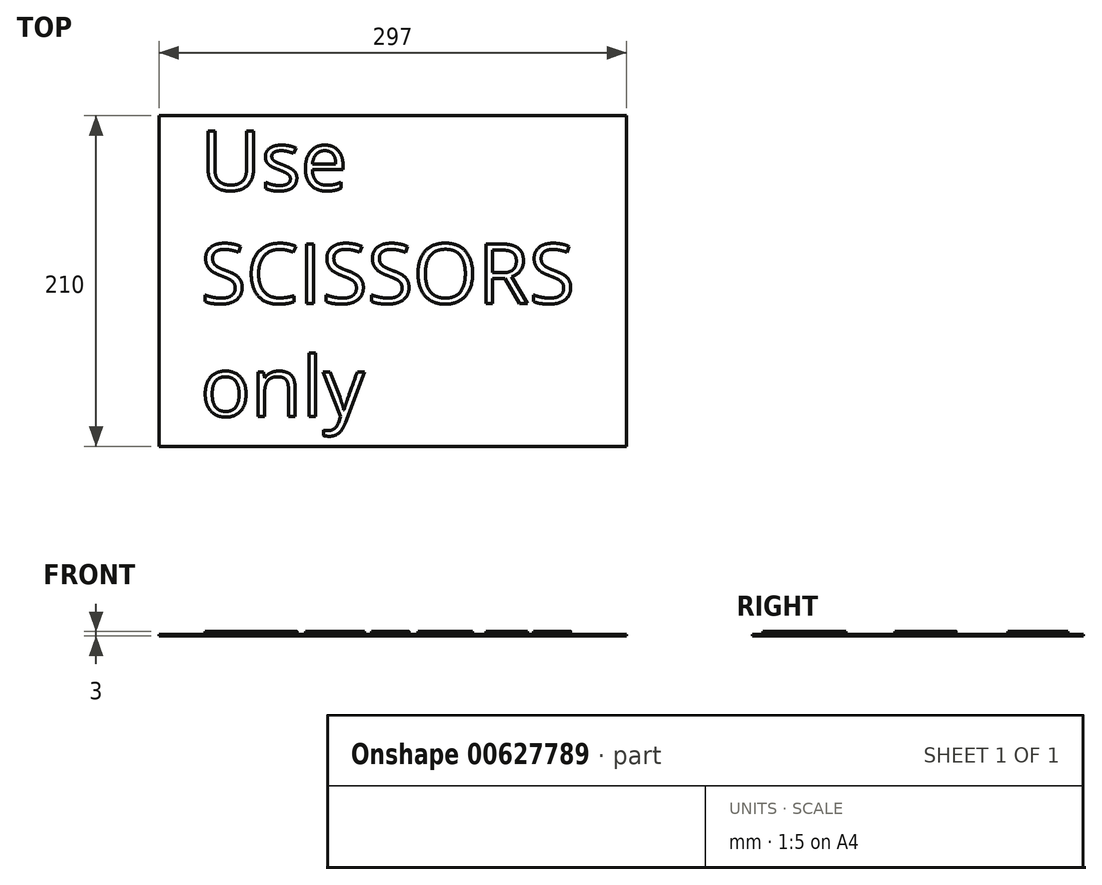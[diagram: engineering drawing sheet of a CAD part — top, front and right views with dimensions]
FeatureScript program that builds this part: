
annotation { "Feature Type Name" : "Feature", "Feature Type Description" : "" }
export const myFeature = defineFeature(function(context is Context, id is Id, definition is map)
    precondition{}
    {
        {
            var Q0;
            Q0=qCreatedBy(makeId("Top.planeOp"),FACE);
            var sketch = newSketch(context, id + "F0", { "sketchPlane" : qUnion([Q0])});
            skLineSegment(sketch, "E0.bottom", {"start": v(-259.32, 190.85) * mm, "end": v(37.68, 190.85) * mm});
            skLineSegment(sketch, "E0.top", {"start": v(-259.32, -19.15) * mm, "end": v(37.68, -19.15) * mm});
            skLineSegment(sketch, "E0.left", {"start": v(-259.32, 190.85) * mm, "end": v(-259.32, -19.15) * mm});
            skLineSegment(sketch, "E0.right", {"start": v(37.68, 190.85) * mm, "end": v(37.68, -19.15) * mm});
            skSolve(sketch);
        }
        {
            var Q0;
            Q0 = qSketchRegion(id + "F0", true);
            extrude(context, id + "F1", {"entities" : qUnion([Q0]), "depth" : 1 * mm, "offsetDistance" : 25 * mm});
        }
        {
            var Q0;
            Q0=makeQuery(id+"F1.opExtrude","CAP_FACE",FACE,{"disambiguationData":[OSD([sQuery(id+"F0.wireOp",EDGE,"E0.bottom"),sQuery(id+"F0.wireOp",EDGE,"E0.top"),sQuery(id+"F0.wireOp",EDGE,"E0.left"),sQuery(id+"F0.wireOp",EDGE,"E0.right")])],"isStart":false});
            var sketch = newSketch(context, id + "F2", { "sketchPlane" : qUnion([Q0])});
            skText(sketch, "E1", { "text": "Use\nSCISSORS\nonly", "fontName": "OpenSans-Regular.ttf"});
            const initialGuessF2  = {"E1": [-0.23298, 0.1435, 1, 0, 0.038]};
            skSetInitialGuess(sketch, initialGuessF2);
            skSolve(sketch);
        }
        {
            var Q0;
            Q0 = qSketchRegion(id + "F2", true);
            extrude(context, id + "F3", {"entities" : qUnion([Q0]), "operationType" : NewBodyOperationType.ADD, "depth" : 2 * mm, "offsetDistance" : 25 * mm});
        }
    });
